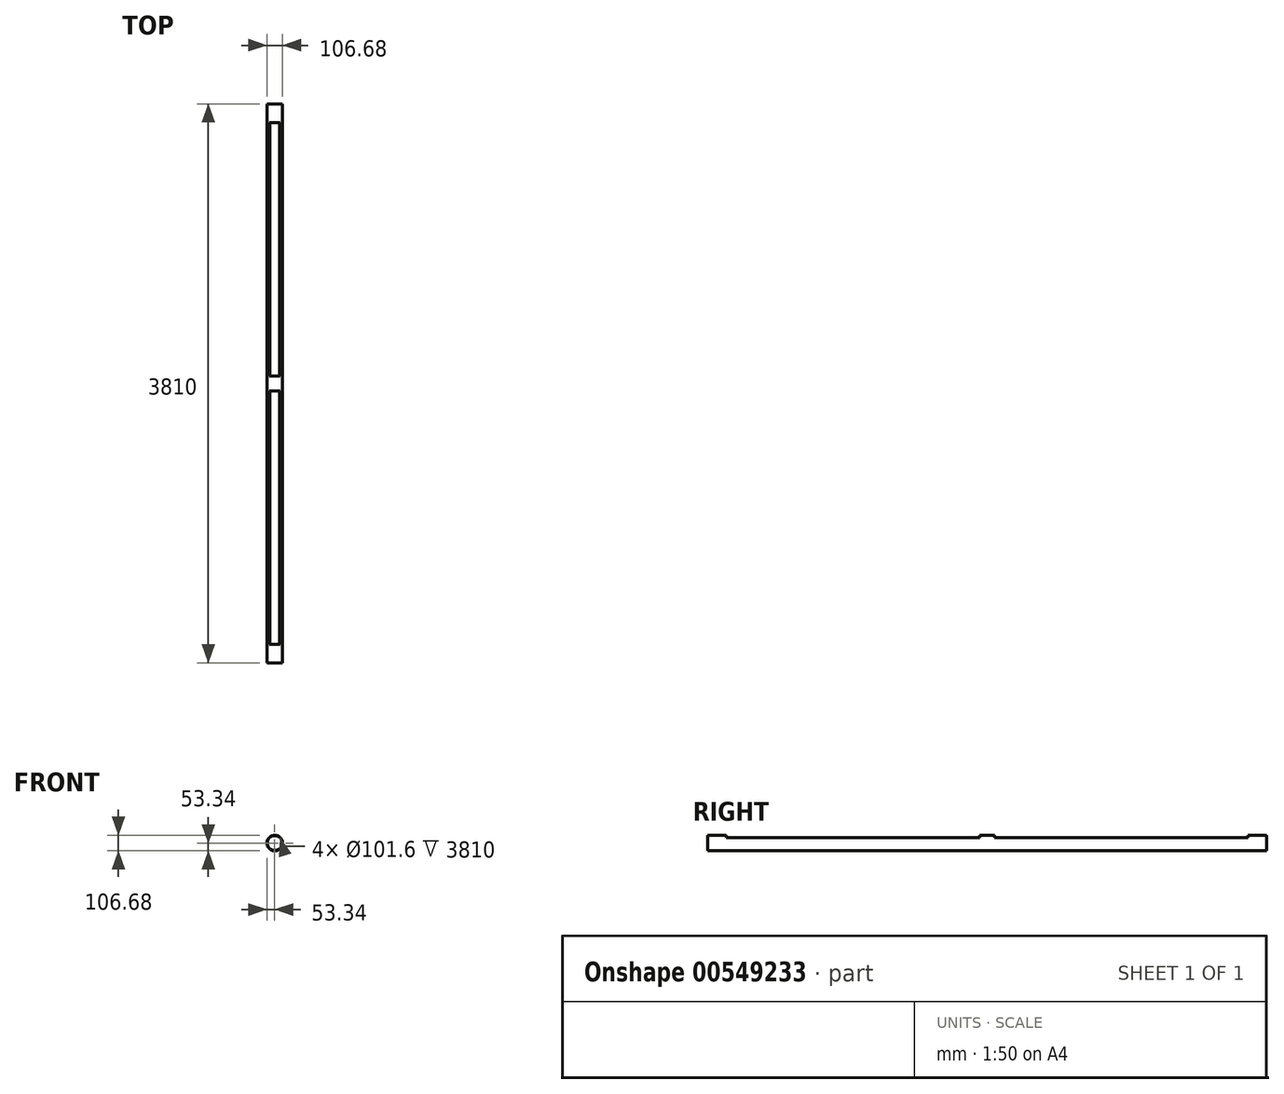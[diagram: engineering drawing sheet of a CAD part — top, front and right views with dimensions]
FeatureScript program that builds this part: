
annotation { "Feature Type Name" : "Feature", "Feature Type Description" : "" }
export const myFeature = defineFeature(function(context is Context, id is Id, definition is map)
    precondition{}
    {
        {
            var Q0;
            Q0=qCreatedBy(makeId("Front.planeOp"),FACE);
            var sketch = newSketch(context, id + "F0", { "sketchPlane" : qUnion([Q0])});
            skCircle(sketch, "E0", {"center": v(0, 0) * mm, "radius": 50.8 * mm});
            skCircle(sketch, "E1", {"center": v(0, 0) * mm, "radius": 53.34 * mm});
            skSolve(sketch);
        }
        {
            var Q0;
            Q0 = qSketchRegion(id + "F0", true);
            extrude(context, id + "F1", {"entities" : qUnion([Q0]), "oppositeDirection" : true, "depth" : 3810 * mm, "offsetDistance" : 25.4 * mm});
        }
        {
            var Q0;
            Q0=qCreatedBy(makeId("Right.planeOp"),FACE);
            var sketch = newSketch(context, id + "F2", { "sketchPlane" : qUnion([Q0])});
            skLineSegment(sketch, "E2", {"start": v(0, 390.76) * mm, "end": v(0, -500.43) * mm, "construction": true});
            skLineSegment(sketch, "E3", {"start": v(3810, -519.58) * mm, "end": v(3810, 558.24) * mm, "construction": true});
            skLineSegment(sketch, "E4", {"start": v(1905, 838.52) * mm, "end": v(1905, -793.8) * mm, "construction": true});
            skLineSegment(sketch, "E5.bottom", {"start": v(127, 298.8) * mm, "end": v(1854.2, 298.8) * mm});
            skLineSegment(sketch, "E5.top", {"start": v(127, 38.1) * mm, "end": v(1854.2, 38.1) * mm});
            skLineSegment(sketch, "E5.left", {"start": v(127, 298.8) * mm, "end": v(127, 38.1) * mm});
            skLineSegment(sketch, "E5.right", {"start": v(1854.2, 298.8) * mm, "end": v(1854.2, 38.1) * mm});
            skLineSegment(sketch, "E6.MirrorCS", {"start": v(3683, 298.8) * mm, "end": v(3683, 38.1) * mm});
            skLineSegment(sketch, "E7.MirrorCS", {"start": v(3683, 38.1) * mm, "end": v(1955.8, 38.1) * mm});
            skLineSegment(sketch, "E8.MirrorCS", {"start": v(3683, 298.8) * mm, "end": v(1955.8, 298.8) * mm});
            skLineSegment(sketch, "E9.MirrorCS", {"start": v(1955.8, 298.8) * mm, "end": v(1955.8, 38.1) * mm});
            skSolve(sketch);
        }
        {
            var Q0;
            Q0=makeQuery(id+"F2.imprint","IMPRINT",FACE,{"disambiguationData":[TD([[makeQuery(id+"F2.imprint","IMPRINT",EDGE,{"derivedFrom":sQuery(id+"F2.wireOp",EDGE,"E5.bottom")}),-1.0]])]});
            var Q1;
            Q1=makeQuery(id+"F2.imprint","IMPRINT",FACE,{"disambiguationData":[TD([[makeQuery(id+"F2.imprint","IMPRINT",EDGE,{"derivedFrom":sQuery(id+"F2.wireOp",EDGE,"E6.MirrorCS")}),-1.0]])]});
            extrude(context, id + "F3", {"entities" : qUnion([Q0, Q1]), "operationType" : NewBodyOperationType.REMOVE, "endBound" : BoundingType.SYMMETRIC, "oppositeDirection" : true, "depth" : 254 * mm, "offsetDistance" : 25.4 * mm});
        }
    });
